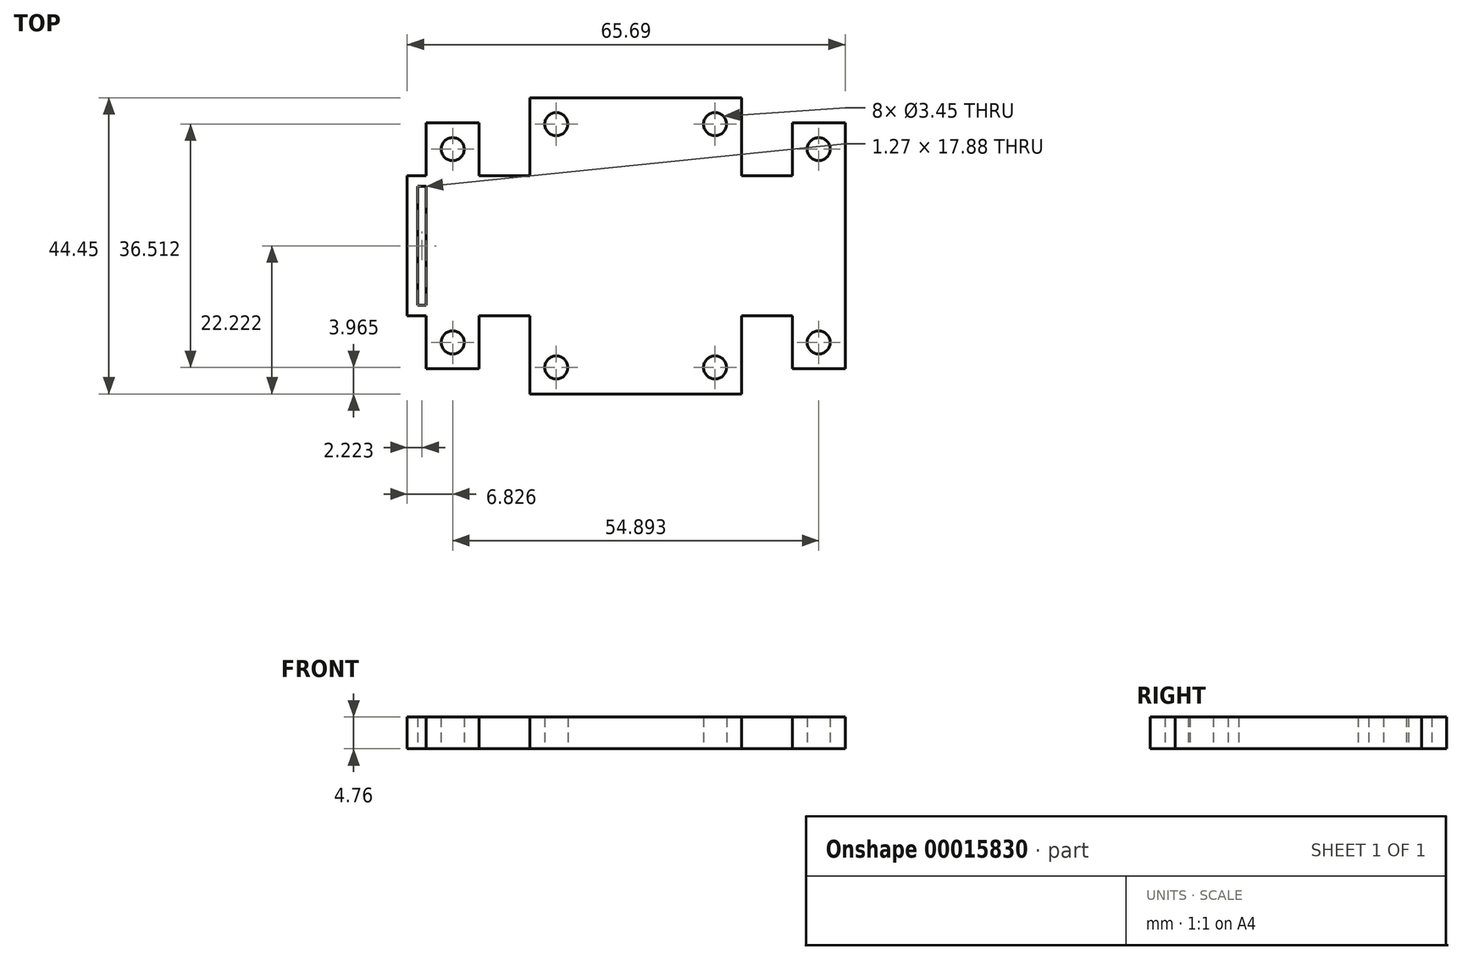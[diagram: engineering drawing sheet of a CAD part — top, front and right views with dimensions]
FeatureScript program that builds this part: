
annotation { "Feature Type Name" : "Feature", "Feature Type Description" : "" }
export const myFeature = defineFeature(function(context is Context, id is Id, definition is map)
    precondition{}
    {
        {
            var Q0;
            Q0=qCreatedBy(makeId("Top.planeOp"),FACE);
            var sketch = newSketch(context, id + "F0", { "sketchPlane" : qUnion([Q0])});
            skLineSegment(sketch, "E0.left", {"start": v(0, 0) * mm, "end": v(0, -21.06) * mm});
            skLineSegment(sketch, "E1", {"start": v(0, -21.06) * mm, "end": v(2.86, -21.06) * mm});
            skLineSegment(sketch, "E2.bottom", {"start": v(2.86, -21.06) * mm, "end": v(10.8, -21.06) * mm, "construction": true});
            skLineSegment(sketch, "E2.top", {"start": v(2.86, -29) * mm, "end": v(10.8, -29) * mm});
            skLineSegment(sketch, "E2.left", {"start": v(2.86, -21.06) * mm, "end": v(2.86, -29) * mm});
            skLineSegment(sketch, "E2.right", {"start": v(10.8, -21.06) * mm, "end": v(10.8, -29) * mm});
            skLineSegment(sketch, "E3.bottom", {"start": v(57.75, -21.06) * mm, "end": v(65.69, -21.06) * mm, "construction": true});
            skLineSegment(sketch, "E3.top", {"start": v(57.75, -29) * mm, "end": v(65.69, -29) * mm});
            skLineSegment(sketch, "E3.left", {"start": v(57.75, -21.06) * mm, "end": v(57.75, -29) * mm});
            skLineSegment(sketch, "E3.right", {"start": v(65.69, -21.06) * mm, "end": v(65.69, -29) * mm});
            skLineSegment(sketch, "E4", {"start": v(0, 0) * mm, "end": v(2.86, 0) * mm});
            skLineSegment(sketch, "E5.bottom", {"start": v(2.86, 0) * mm, "end": v(10.8, 0) * mm, "construction": true});
            skLineSegment(sketch, "E5.top", {"start": v(2.86, 7.94) * mm, "end": v(10.8, 7.94) * mm});
            skLineSegment(sketch, "E5.left", {"start": v(2.86, 0) * mm, "end": v(2.86, 7.94) * mm});
            skLineSegment(sketch, "E5.right", {"start": v(10.8, 0) * mm, "end": v(10.8, 7.94) * mm});
            skLineSegment(sketch, "E6.bottom", {"start": v(57.75, 0) * mm, "end": v(65.69, 0) * mm, "construction": true});
            skLineSegment(sketch, "E6.top", {"start": v(57.75, 7.94) * mm, "end": v(65.69, 7.94) * mm});
            skLineSegment(sketch, "E6.left", {"start": v(57.75, 0) * mm, "end": v(57.75, 7.94) * mm});
            skLineSegment(sketch, "E6.right", {"start": v(65.69, 0) * mm, "end": v(65.69, 7.94) * mm});
            skLineSegment(sketch, "E7", {"start": v(6.83, 7.94) * mm, "end": v(6.83, 3.97) * mm});
            skLineSegment(sketch, "E8", {"start": v(61.72, 7.94) * mm, "end": v(61.72, 3.97) * mm});
            skLineSegment(sketch, "E9", {"start": v(6.83, -29) * mm, "end": v(6.83, -25.03) * mm});
            skLineSegment(sketch, "E10", {"start": v(61.72, -29) * mm, "end": v(61.72, -25.03) * mm});
            skCircle(sketch, "E11", {"center": v(61.72, 3.97) * mm, "radius": 1.73 * mm});
            skCircle(sketch, "E12", {"center": v(6.83, 3.97) * mm, "radius": 1.73 * mm});
            skCircle(sketch, "E13", {"center": v(61.72, -25.03) * mm, "radius": 1.73 * mm});
            skCircle(sketch, "E14", {"center": v(6.83, -25.03) * mm, "radius": 1.73 * mm});
            skLineSegment(sketch, "E15", {"start": v(0, -10.53) * mm, "end": v(1.59, -10.53) * mm, "construction": true});
            skLineSegment(sketch, "E16.bottom", {"start": v(1.59, -19.47) * mm, "end": v(2.86, -19.47) * mm});
            skLineSegment(sketch, "E16.top", {"start": v(1.59, -1.59) * mm, "end": v(2.86, -1.59) * mm});
            skLineSegment(sketch, "E16.left", {"start": v(1.59, -19.47) * mm, "end": v(1.59, -1.59) * mm});
            skLineSegment(sketch, "E16.right", {"start": v(2.86, -19.47) * mm, "end": v(2.86, -1.59) * mm});
            skLineSegment(sketch, "E17", {"start": v(1.59, -1.59) * mm, "end": v(1.59, 0) * mm, "construction": true});
            skLineSegment(sketch, "E18", {"start": v(65.69, 0) * mm, "end": v(65.69, -21.06) * mm});
            skLineSegment(sketch, "E19", {"start": v(10.8, -21.06) * mm, "end": v(18.4, -21.06) * mm});
            skLineSegment(sketch, "E20", {"start": v(57.75, -21.06) * mm, "end": v(50.15, -21.06) * mm});
            skLineSegment(sketch, "E21.bottom", {"start": v(18.4, -21.06) * mm, "end": v(50.15, -21.06) * mm, "construction": true});
            skLineSegment(sketch, "E21.top", {"start": v(18.4, -32.75) * mm, "end": v(50.15, -32.75) * mm});
            skLineSegment(sketch, "E21.left", {"start": v(18.4, -21.06) * mm, "end": v(18.4, -32.75) * mm});
            skLineSegment(sketch, "E21.right", {"start": v(50.15, -21.06) * mm, "end": v(50.15, -32.75) * mm});
            skLineSegment(sketch, "E22", {"start": v(22.37, -32.75) * mm, "end": v(22.37, -28.78) * mm, "construction": true});
            skLineSegment(sketch, "E23", {"start": v(22.37, -28.78) * mm, "end": v(18.4, -28.78) * mm, "construction": true});
            skLineSegment(sketch, "E24", {"start": v(46.18, -32.75) * mm, "end": v(46.18, -28.78) * mm, "construction": true});
            skLineSegment(sketch, "E25", {"start": v(46.18, -28.78) * mm, "end": v(50.15, -28.78) * mm, "construction": true});
            skLineSegment(sketch, "E26", {"start": v(10.8, 0) * mm, "end": v(18.4, 0) * mm});
            skLineSegment(sketch, "E27", {"start": v(57.75, 0) * mm, "end": v(50.15, 0) * mm});
            skLineSegment(sketch, "E28.bottom", {"start": v(18.4, 0) * mm, "end": v(50.15, 0) * mm, "construction": true});
            skLineSegment(sketch, "E28.top", {"start": v(18.4, 11.7) * mm, "end": v(50.15, 11.7) * mm});
            skLineSegment(sketch, "E28.left", {"start": v(18.4, 0) * mm, "end": v(18.4, 11.7) * mm});
            skLineSegment(sketch, "E28.right", {"start": v(50.15, 0) * mm, "end": v(50.15, 11.7) * mm});
            skLineSegment(sketch, "E29", {"start": v(22.37, 11.7) * mm, "end": v(22.37, 7.73) * mm, "construction": true});
            skLineSegment(sketch, "E30", {"start": v(46.18, 11.7) * mm, "end": v(46.18, 7.73) * mm, "construction": true});
            skCircle(sketch, "E31", {"center": v(46.18, 7.73) * mm, "radius": 1.73 * mm});
            skCircle(sketch, "E32", {"center": v(22.37, 7.73) * mm, "radius": 1.73 * mm});
            skCircle(sketch, "E33", {"center": v(46.18, -28.78) * mm, "radius": 1.73 * mm});
            skCircle(sketch, "E34", {"center": v(22.37, -28.78) * mm, "radius": 1.73 * mm});
            skSolve(sketch);
        }
        {
            var Q0;
            Q0=qSketchRegion(id+"F0",true);
            extrude(context, id + "F1", {"entities" : qUnion([Q0]), "depth" : 4.76 * mm});
        }
    });
